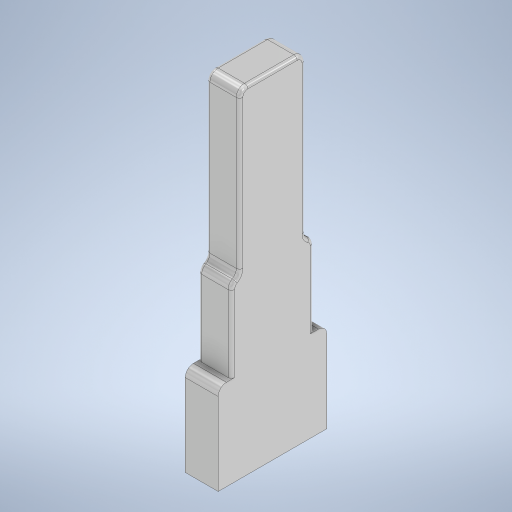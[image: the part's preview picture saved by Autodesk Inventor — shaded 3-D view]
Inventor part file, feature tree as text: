
AUTODESK INVENTOR PART (.ipt)
format: ipt  version: 2023 (Build 270158000, 158)  size: 283,648 bytes
history: native  units: in
note: dims shown in document units (in); Inventor stores cm internally (conversion verified against a paired STEP export)
features: fillet x2, extrude x1, sketch x1
ambient origin geometry x8: Origin, YZ Plane, XZ Plane, XY Plane, X Axis, Y Axis, Z Axis, Center Point
bodies: Solid1 (feature_tree)
feature tree (4):
  extrude  "Extrusion1"  Depth=0.2165in
  fillet  "Fillet1"  Radius=0.1969in
  fillet  "Fillet2"  Radius=0.1575in
  sketch  "Sketch4"  dims[d0=0.2598in d1=0.2165in d2=0.1969in d3=0.1575in d4=0.5906in d5=0.3937in d6=0.0787in d7=0.0in d8=0.0197in d9=0.0079in]
